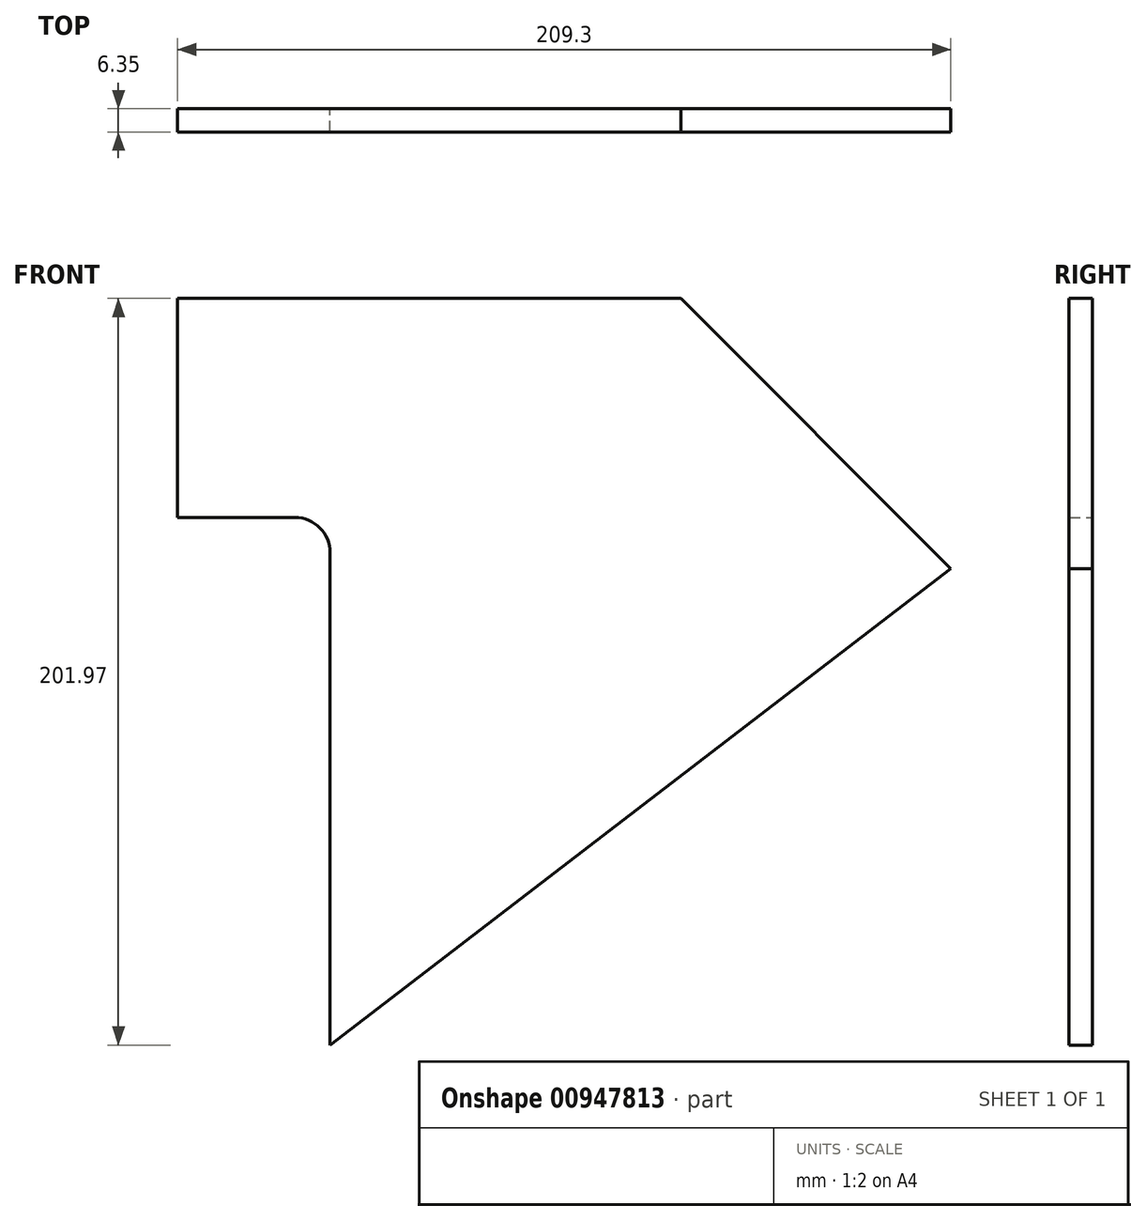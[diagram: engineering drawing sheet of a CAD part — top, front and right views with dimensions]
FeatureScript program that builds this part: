
annotation { "Feature Type Name" : "Feature", "Feature Type Description" : "" }
export const myFeature = defineFeature(function(context is Context, id is Id, definition is map)
    precondition{}
    {
        {
            var Q0;
            Q0=qCreatedBy(makeId("Front.planeOp"),FACE);
            var sketch = newSketch(context, id + "F0", { "sketchPlane" : qUnion([Q0])});
            skLineSegment(sketch, "E0", {"start": v(136.2, 0) * mm, "end": v(209.3, -73.1) * mm});
            skLineSegment(sketch, "E1", {"start": v(209.3, -73.1) * mm, "end": v(41.27, -201.97) * mm});
            skLineSegment(sketch, "E2", {"start": v(41.27, -201.97) * mm, "end": v(41.27, -68.76) * mm});
            skLineSegment(sketch, "E3", {"start": v(31.75, -59.24) * mm, "end": v(0, -59.24) * mm});
            skLineSegment(sketch, "E4", {"start": v(0, -59.24) * mm, "end": v(0, 0) * mm});
            skLineSegment(sketch, "E5", {"start": v(0, 0) * mm, "end": v(136.2, 0) * mm});
            skArc(sketch, "E6", {"start": v(41.27, -68.76) * mm, "mid": v(38.49, -62.03) * mm, "end": v(31.75, -59.24) * mm});
            skSolve(sketch);
        }
        {
            var Q0;
            Q0 = qSketchRegion(id + "F0", true);
            extrude(context, id + "F1", {"entities" : qUnion([Q0]), "depth" : 6.35 * mm, "offsetDistance" : 25 * mm});
        }
    });
